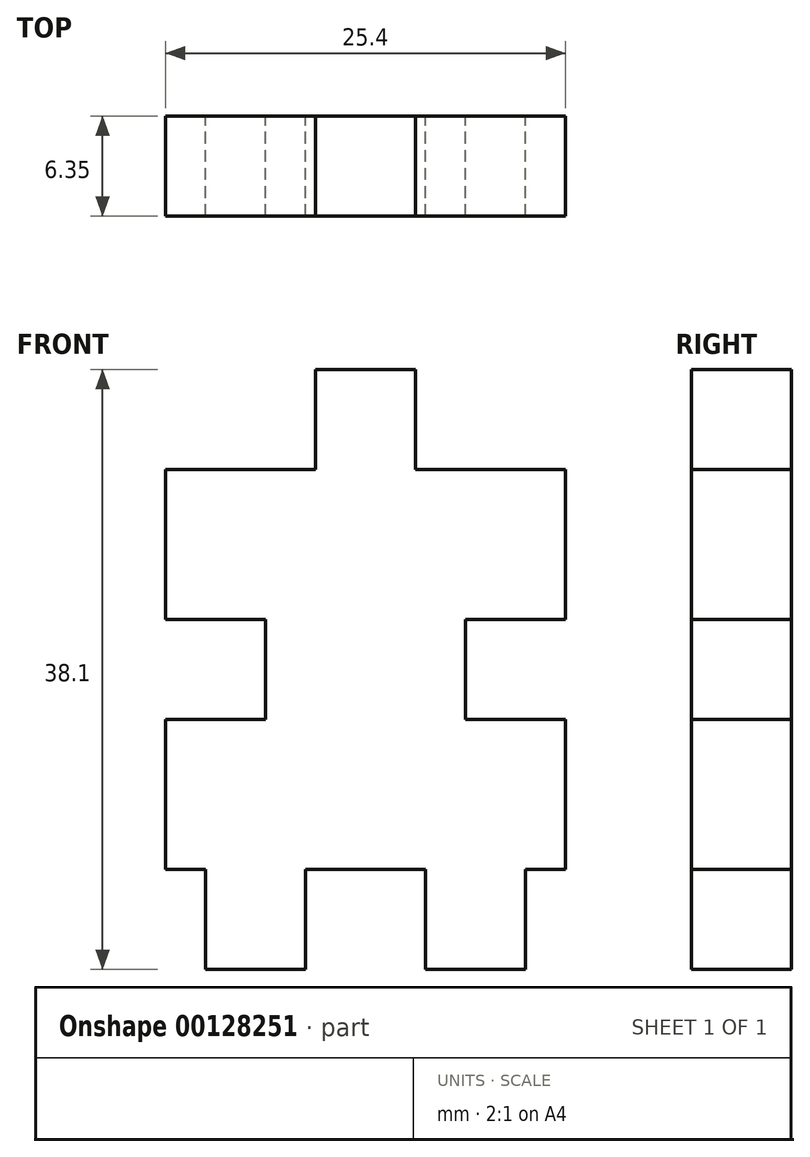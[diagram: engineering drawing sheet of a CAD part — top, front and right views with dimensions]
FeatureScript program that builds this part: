
annotation { "Feature Type Name" : "Feature", "Feature Type Description" : "" }
export const myFeature = defineFeature(function(context is Context, id is Id, definition is map)
    precondition{}
    {
        {
            var Q0;
            Q0=qCreatedBy(makeId("Front.planeOp"),FACE);
            var sketch = newSketch(context, id + "F0", { "sketchPlane" : qUnion([Q0])});
            skLineSegment(sketch, "E0.bottom", {"start": v(-12.7, 15.35) * mm, "end": v(12.7, 15.35) * mm});
            skLineSegment(sketch, "E0.top", {"start": v(-12.7, -10.05) * mm, "end": v(12.7, -10.05) * mm});
            skLineSegment(sketch, "E0.left", {"start": v(-12.7, 15.35) * mm, "end": v(-12.7, -10.05) * mm});
            skLineSegment(sketch, "E0.right", {"start": v(12.7, 15.35) * mm, "end": v(12.7, -10.05) * mm});
            skLineSegment(sketch, "E1.bottom", {"start": v(-10.16, -10.05) * mm, "end": v(-3.8, -10.05) * mm});
            skLineSegment(sketch, "E1.top", {"start": v(-10.16, -16.4) * mm, "end": v(-3.8, -16.4) * mm});
            skLineSegment(sketch, "E1.left", {"start": v(-10.16, -10.05) * mm, "end": v(-10.16, -16.4) * mm});
            skLineSegment(sketch, "E1.right", {"start": v(-3.8, -10.05) * mm, "end": v(-3.8, -16.4) * mm});
            skLineSegment(sketch, "E2.bottom", {"start": v(10.16, -10.05) * mm, "end": v(3.8, -10.05) * mm});
            skLineSegment(sketch, "E2.top", {"start": v(10.16, -16.4) * mm, "end": v(3.8, -16.4) * mm});
            skLineSegment(sketch, "E2.left", {"start": v(10.16, -10.05) * mm, "end": v(10.16, -16.4) * mm});
            skLineSegment(sketch, "E2.right", {"start": v(3.81, -10.05) * mm, "end": v(3.81, -16.4) * mm});
            skLineSegment(sketch, "E3.bottom", {"start": v(-3.17, 15.35) * mm, "end": v(3.18, 15.35) * mm});
            skLineSegment(sketch, "E3.top", {"start": v(-3.17, 21.7) * mm, "end": v(3.18, 21.7) * mm});
            skLineSegment(sketch, "E3.left", {"start": v(-3.17, 15.35) * mm, "end": v(-3.17, 21.7) * mm});
            skLineSegment(sketch, "E3.right", {"start": v(3.18, 15.35) * mm, "end": v(3.18, 21.7) * mm});
            skLineSegment(sketch, "E4.bottom", {"start": v(-12.7, -0.53) * mm, "end": v(-6.35, -0.53) * mm});
            skLineSegment(sketch, "E4.top", {"start": v(-12.7, 5.82) * mm, "end": v(-6.35, 5.82) * mm});
            skLineSegment(sketch, "E4.left", {"start": v(-12.7, -0.53) * mm, "end": v(-12.7, 5.82) * mm});
            skLineSegment(sketch, "E4.right", {"start": v(-6.35, -0.53) * mm, "end": v(-6.35, 5.82) * mm});
            skLineSegment(sketch, "E5.bottom", {"start": v(12.7, -0.53) * mm, "end": v(6.35, -0.53) * mm});
            skLineSegment(sketch, "E5.top", {"start": v(12.7, 5.82) * mm, "end": v(6.35, 5.82) * mm});
            skLineSegment(sketch, "E5.left", {"start": v(12.7, -0.53) * mm, "end": v(12.7, 5.82) * mm});
            skLineSegment(sketch, "E5.right", {"start": v(6.35, -0.53) * mm, "end": v(6.35, 5.82) * mm});
            skSolve(sketch);
        }
        {
            var Q0;
            Q0 = qSketchRegion(id + "F0", true);
            extrude(context, id + "F1", {"entities" : qUnion([Q0]), "depth" : 6.35 * mm});
        }
        {
            var Q0;
            Q0=makeQuery(id+"F0.imprint","IMPRINT",FACE,{"disambiguationData":[TD([[makeQuery(id+"F0.imprint","IMPRINT",EDGE,{"derivedFrom":sQuery(id+"F0.wireOp",EDGE,"E4.bottom")}),1.0]])]});
            var Q1;
            Q1=makeQuery(id+"F0.imprint","IMPRINT",FACE,{"disambiguationData":[TD([[makeQuery(id+"F0.imprint","IMPRINT",EDGE,{"derivedFrom":sQuery(id+"F0.wireOp",EDGE,"E5.bottom")}),-1.0]])]});
            extrude(context, id + "F2", {"entities" : qUnion([Q0, Q1]), "operationType" : NewBodyOperationType.REMOVE, "depth" : 6.35 * mm});
        }
    });
